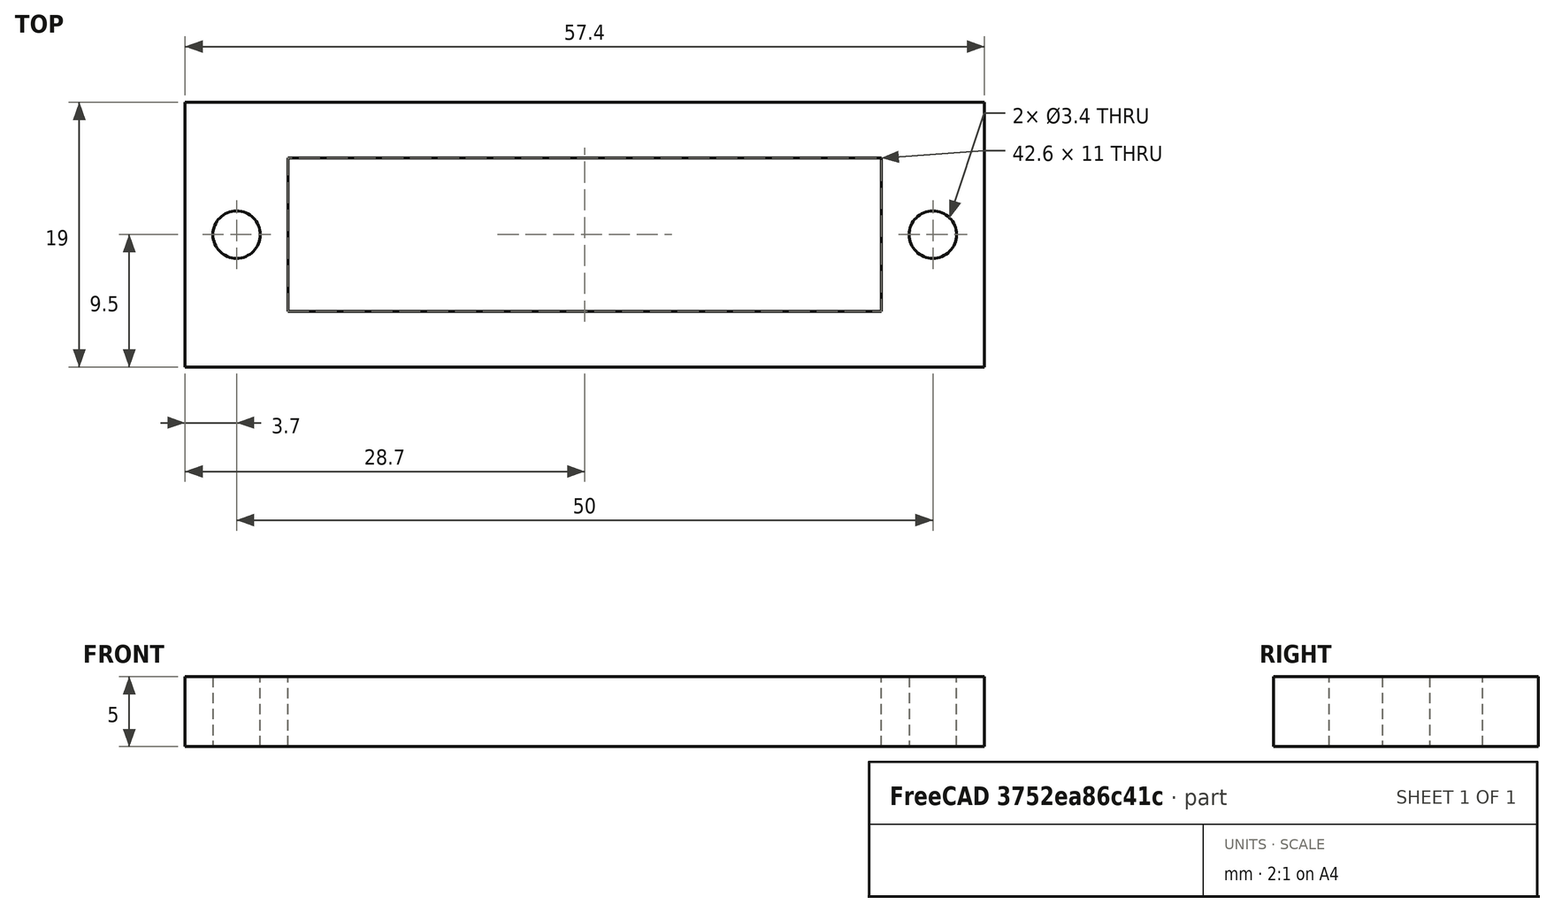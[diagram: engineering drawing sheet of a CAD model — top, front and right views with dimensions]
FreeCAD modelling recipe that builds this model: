
FCSTD DOCUMENT  (FreeCAD 1.0R39109 (Git))
Label: Switch bracket
License: Creative Commons Attribution-ShareAlike 4.0
LicenseURL: https://creativecommons.org/licenses/by-sa/4.0/
objects: Sketcher::SketchObject×1, PartDesign::Pad×1, PartDesign::Body×1
note: 6 computed .brp shape members not serialized (recipe doc carries the construction recipe); baked Part::Feature solids carry a one-line shape summary decoded from their .brp

FEATURE [Sketcher::SketchObject] Sketch
  ArcFitTolerance = 1e-06
  AttachmentSupport = -> [XY_Plane]
  FullyConstrained = true
  MakeInternals = false
  MapMode = 5
  sketch-geometry (12):
    g0: Circle CenterX=-25 CenterY=0 CenterZ=0 NormalX=0 NormalY=0 NormalZ=1 AngleXU=0 Radius=1.7
    g1: Circle CenterX=25 CenterY=0 CenterZ=0 NormalX=0 NormalY=0 NormalZ=1 AngleXU=0 Radius=1.7
    g2: LineSegment StartX=-28.7 StartY=9.5 StartZ=0 EndX=-28.7 EndY=-9.5 EndZ=0
    g3: LineSegment StartX=-28.7 StartY=-9.5 StartZ=0 EndX=28.7 EndY=-9.5 EndZ=0
    g4: LineSegment StartX=28.7 StartY=-9.5 StartZ=0 EndX=28.7 EndY=9.5 EndZ=0
    g5: LineSegment StartX=28.7 StartY=9.5 StartZ=0 EndX=-28.7 EndY=9.5 EndZ=0
    g6: GeomPoint [constr] X=0 Y=0 Z=0
    g7: LineSegment StartX=-21.3 StartY=5.5 StartZ=0 EndX=-21.3 EndY=-5.5 EndZ=0
    g8: LineSegment StartX=-21.3 StartY=-5.5 StartZ=0 EndX=21.3 EndY=-5.5 EndZ=0
    g9: LineSegment StartX=21.3 StartY=-5.5 StartZ=0 EndX=21.3 EndY=5.5 EndZ=0
    g10: LineSegment StartX=21.3 StartY=5.5 StartZ=0 EndX=-21.3 EndY=5.5 EndZ=0
    g11: GeomPoint [constr] X=0 Y=0 Z=0
  constraints (29):
    c: PointOnObject(g0,g-1)
    c: Diameter(g0) = 3.4
    c: Symmetric(g1,g0,g-2)
    c: DistanceX(g0,g1) = 50
    c: Coincident(g2,g3)
    c: Coincident(g3,g4)
    c: Coincident(g4,g5)
    c: Coincident(g5,g2)
    c: Vertical(g2)
    c: Vertical(g4)
    c: Horizontal(g3)
    c: Horizontal(g5)
    c: Symmetric(g4,g2,g6)
    c: Coincident(g6,g-1)
    c: DistanceY(g4,g4) = 19
    c: DistanceX(g1,g3) = 3.7
    c: Equal(g1,g0)
    c: Coincident(g7,g8)
    c: Coincident(g8,g9)
    c: Coincident(g9,g10)
    c: Coincident(g10,g7)
    c: Vertical(g7)
    c: Vertical(g9)
    c: Horizontal(g8)
    c: Horizontal(g10)
    c: Symmetric(g9,g7,g11)
    c: Coincident(g11,g6)
    c: DistanceY(g9,g9) = 11
    c: DistanceX(g8,g1) = 3.7
FEATURE [PartDesign::Pad] Pad
  Direction = (0,0,1)
  Length = 5
  Length2 = 10
  Profile = -> Sketch
  ReferenceAxis = -> Sketch [N_Axis]
  Suppressed = false
  Type = 0
FEATURE [PartDesign::Body] Body
  AllowCompound = false
  Group = -> [Sketch,Pad]
  Origin = -> Origin
  Tip = -> Pad
